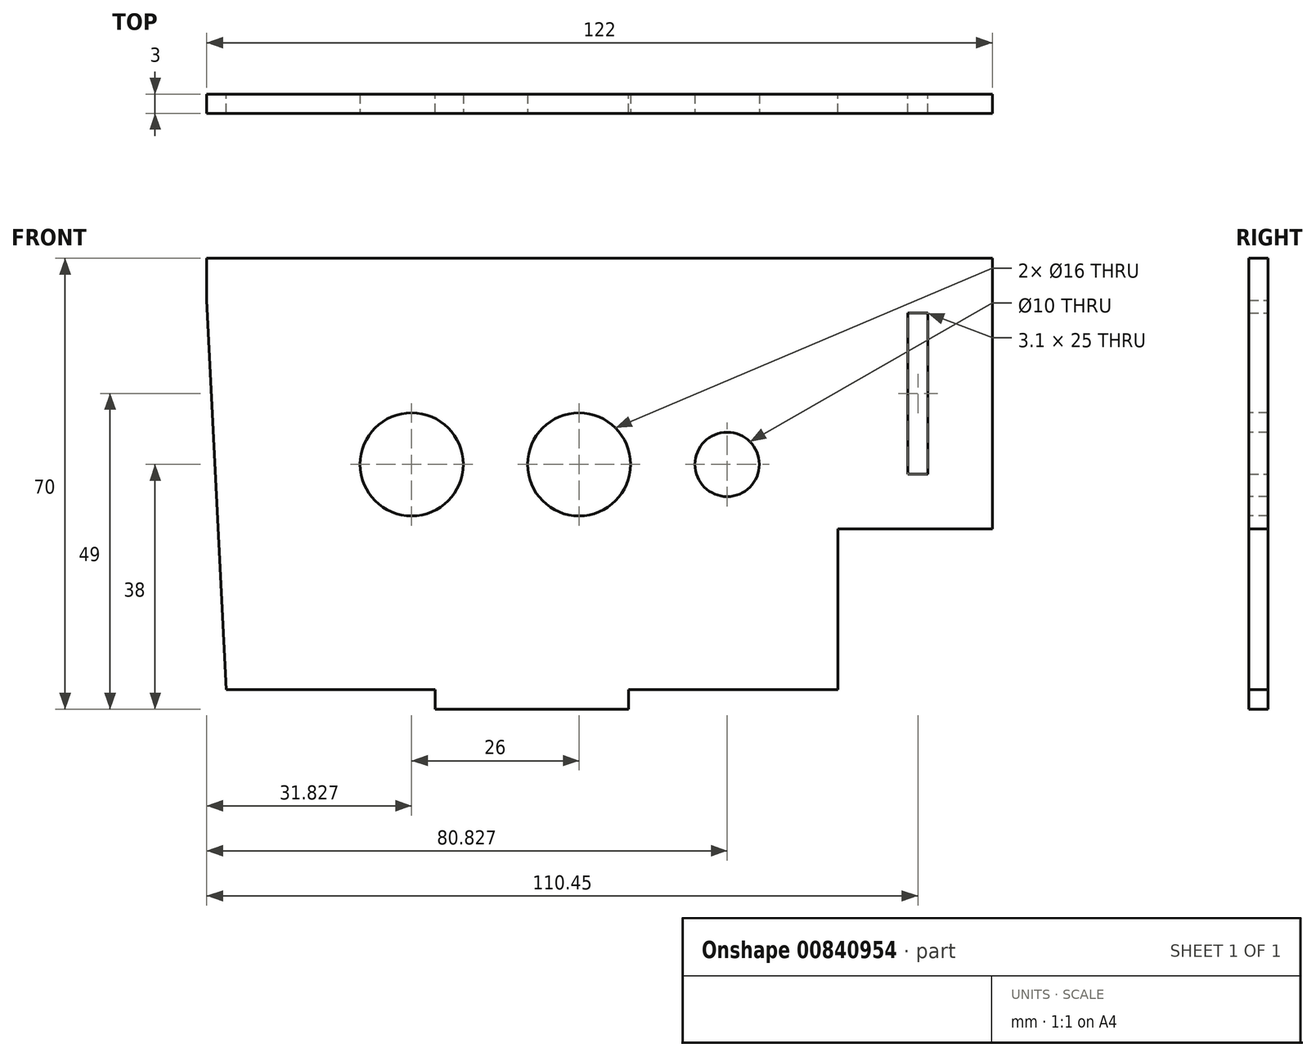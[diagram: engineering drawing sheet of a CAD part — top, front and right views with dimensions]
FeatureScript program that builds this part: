
annotation { "Feature Type Name" : "Feature", "Feature Type Description" : "" }
export const myFeature = defineFeature(function(context is Context, id is Id, definition is map)
    precondition{}
    {
        {
            var Q0;
            Q0=qCreatedBy(makeId("Front.planeOp"),FACE);
            var sketch = newSketch(context, id + "F0", { "sketchPlane" : qUnion([Q0])});
            skLineSegment(sketch, "E0", {"start": v(44.72, 6.5) * mm, "end": v(68.72, 6.5) * mm});
            skLineSegment(sketch, "E1", {"start": v(68.72, 6.5) * mm, "end": v(68.72, -35.5) * mm});
            skLineSegment(sketch, "E2", {"start": v(68.72, -35.5) * mm, "end": v(44.72, -35.5) * mm});
            skLineSegment(sketch, "E3", {"start": v(44.72, -35.5) * mm, "end": v(44.72, -60.5) * mm});
            skLineSegment(sketch, "E4", {"start": v(-50.28, 6.5) * mm, "end": v(44.72, 6.5) * mm});
            skLineSegment(sketch, "E5", {"start": v(-50.28, -60.5) * mm, "end": v(44.72, -60.5) * mm});
            skLineSegment(sketch, "E6", {"start": v(-50.28, 6.5) * mm, "end": v(-53.28, 6.5) * mm});
            skLineSegment(sketch, "E7", {"start": v(-53.28, 6.5) * mm, "end": v(-53.28, 0) * mm});
            skLineSegment(sketch, "E8", {"start": v(-53.28, 0) * mm, "end": v(-50.28, -60.5) * mm});
            skLineSegment(sketch, "E9", {"start": v(-2.78, -60.5) * mm, "end": v(-2.78, 6.5) * mm, "construction": true});
            skLineSegment(sketch, "E10.bottom", {"start": v(-17.78, -60.5) * mm, "end": v(12.22, -60.5) * mm});
            skLineSegment(sketch, "E10.top", {"start": v(-17.78, -63.5) * mm, "end": v(12.22, -63.5) * mm});
            skLineSegment(sketch, "E10.left", {"start": v(-17.78, -60.5) * mm, "end": v(-17.78, -63.5) * mm});
            skLineSegment(sketch, "E10.right", {"start": v(12.22, -60.5) * mm, "end": v(12.22, -63.5) * mm});
            skSolve(sketch);
        }
        {
            var Q0;
            Q0 = qSketchRegion(id + "F0", true);
            extrude(context, id + "F1", {"entities" : qUnion([Q0]), "depth" : 3 * mm, "offsetDistance" : 25 * mm});
        }
        {
            var Q0;
            Q0=makeQuery(id+"F1.opExtrude","CAP_FACE",FACE,{"disambiguationData":[OSD([sQuery(id+"F0.wireOp",EDGE,"3fbb6350-39d0-430e-a766-6ca8a1800e6b"),sQuery(id+"F0.wireOp",EDGE,"8caad027-3218-4afd-bd4f-54f93bda641c"),sQuery(id+"F0.wireOp",EDGE,"E0"),sQuery(id+"F0.wireOp",EDGE,"E1"),sQuery(id+"F0.wireOp",EDGE,"E2"),sQuery(id+"F0.wireOp",EDGE,"E3"),sQuery(id+"F0.wireOp",EDGE,"95b40326-b849-479a-8954-89840e513a77"),sQuery(id+"F0.wireOp",EDGE,"E4")])],"isStart":true});
            var sketch = newSketch(context, id + "F2", { "sketchPlane" : qUnion([Q0])});
            skLineSegment(sketch, "E11.bottom", {"start": v(-58.72, -2) * mm, "end": v(-55.62, -2) * mm});
            skLineSegment(sketch, "E11.top", {"start": v(-58.72, -27) * mm, "end": v(-55.62, -27) * mm});
            skLineSegment(sketch, "E11.left", {"start": v(-58.72, -2) * mm, "end": v(-58.72, -27) * mm});
            skLineSegment(sketch, "E11.right", {"start": v(-55.62, -2) * mm, "end": v(-55.62, -27) * mm});
            skSolve(sketch);
        }
        {
            var Q0;
            Q0 = qSketchRegion(id + "F2", true);
            extrude(context, id + "F3", {"entities" : qUnion([Q0]), "operationType" : NewBodyOperationType.REMOVE, "oppositeDirection" : true, "depth" : 25 * mm, "offsetDistance" : 25 * mm});
        }
        {
            var Q0;
            Q0=makeQuery(id+"F1.opExtrude","CAP_FACE",FACE,{"disambiguationData":[OSD([sQuery(id+"F0.wireOp",EDGE,"E0"),sQuery(id+"F0.wireOp",EDGE,"E1"),sQuery(id+"F0.wireOp",EDGE,"E2"),sQuery(id+"F0.wireOp",EDGE,"E3"),sQuery(id+"F0.wireOp",EDGE,"E4"),sQuery(id+"F0.wireOp",EDGE,"iXOeCFsf-kNy5-GdPO-tdTj-YHKOwL805YMD"),sQuery(id+"F0.wireOp",EDGE,"E5")])],"isStart":false});
            var sketch = newSketch(context, id + "F4", { "sketchPlane" : qUnion([Q0])});
            skCircle(sketch, "E12", {"center": v(-21.45, -25.5) * mm, "radius": 8 * mm});
            skCircle(sketch, "E13", {"center": v(4.55, -25.5) * mm, "radius": 8 * mm});
            skCircle(sketch, "E14", {"center": v(27.55, -25.5) * mm, "radius": 5 * mm});
            skSolve(sketch);
        }
        {
            var Q0;
            Q0 = qSketchRegion(id + "F4", true);
            extrude(context, id + "F5", {"entities" : qUnion([Q0]), "operationType" : NewBodyOperationType.REMOVE, "oppositeDirection" : true, "depth" : 25 * mm, "offsetDistance" : 25 * mm});
        }
    });
